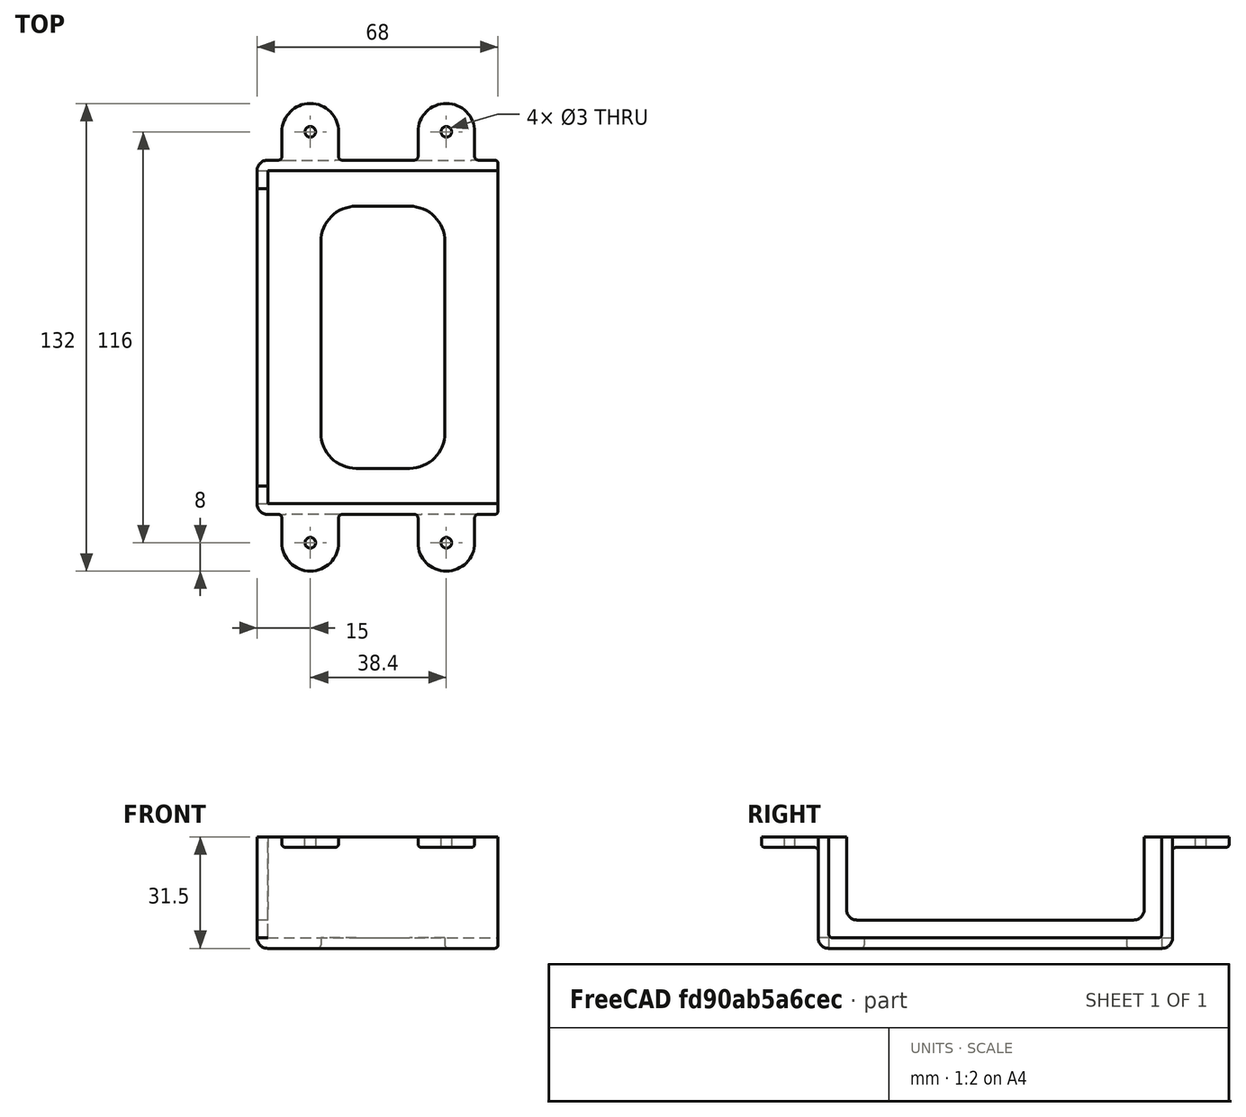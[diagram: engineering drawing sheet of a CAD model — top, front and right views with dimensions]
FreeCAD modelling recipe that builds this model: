
FCSTD DOCUMENT  (FreeCAD 0.21R33668 +7 (Git))
Label: UnderTableBracket-4
License: All rights reserved
LicenseURL: http://en.wikipedia.org/wiki/All_rights_reserved
objects: Sketcher::SketchObject×3, PartDesign::Pocket×2, PartDesign::Fillet×2, Spreadsheet::Sheet×1, PartDesign::AdditiveBox×1, PartDesign::Thickness×1, PartDesign::LinearPattern×1, PartDesign::Plane×1, PartDesign::Mirrored×1, PartDesign::Pad×1, PartDesign::MultiTransform×1, PartDesign::Body×1, App::Part×1, Mesh::Feature×1
note: 22 computed .brp shape members not serialized (recipe doc carries the construction recipe); baked Part::Feature solids carry a one-line shape summary decoded from their .brp

FEATURE [Spreadsheet::Sheet] Spreadsheet
  cells = A1='Width; B1(Width)=94; A2='Height; B2(Height)=28.5; A3='Depth; B3(Depth)=65; A4='Screw Diameter; B4(ScrewDiameter)=3
FEATURE [PartDesign::AdditiveBox] Box
  AttacherType = Attacher::AttachEngine3D
  Height = 28.5
  Length = 65
  Width = 94
  expr: Height = Spreadsheet.Height
  expr: Length = Spreadsheet.Depth
  expr: Width = Spreadsheet.Width
FEATURE [PartDesign::Thickness] Thickness
  Base = -> Box [Face6,Face2]
  BaseFeature = -> Box
  Intersection = false
  Join = 0
  Mode = 0
  SupportTransform = false
  Value = 3
FEATURE [Sketcher::SketchObject] Sketch
  ExternalGeometry = -> [Thickness]
  FullyConstrained = false
  MapMode = 5
  Placement = pos=(0,0,0) rot=(0.57735,0.57735,0.57735;2.0944rad)
  Support = -> [Thickness]
  sketch-geometry (8):
    g0: LineSegment StartX=89 StartY=28.5 StartZ=0 EndX=89 EndY=8 EndZ=0
    g1: ArcOfCircle CenterX=86 CenterY=8 CenterZ=0 NormalX=0 NormalY=0 NormalZ=1 AngleXU=0 Radius=3 StartAngle=4.71239 EndAngle=6.28319
    g2: LineSegment StartX=86 StartY=5 StartZ=0 EndX=8 EndY=5 EndZ=0
    g3: ArcOfCircle CenterX=8 CenterY=8 CenterZ=0 NormalX=0 NormalY=0 NormalZ=1 AngleXU=0 Radius=3 StartAngle=3.14159 EndAngle=4.71239
    g4: LineSegment StartX=5 StartY=8 StartZ=0 EndX=5 EndY=28.5 EndZ=0
    g5: GeomPoint X=5 Y=35.516 Z=0
    g6: GeomPoint X=89 Y=5 Z=0
    g7: LineSegment StartX=5 StartY=28.5 StartZ=0 EndX=89 EndY=28.5 EndZ=0
  constraints (19):
    c: Tangent(g0,g1) = 1.5708
    c: Tangent(g1,g2) = 1.5708
    c: Tangent(g2,g3) = 1.5708
    c: Tangent(g3,g4) = 1.5708
    c: Horizontal(g2)
    c: Vertical(g0)
    c: Vertical(g4)
    c: Equal(g1,g3)
    c: PointOnObject(g5,g4)
    c: PointOnObject(g6,g0)
    c: PointOnObject(g6,g2)
    c: PointOnObject(g4,g-3)
    c: PointOnObject(g0,g-3)
    c: Radius(g3) = 3
    c: DistanceX(g-3,g4) = 5
    c: DistanceX(g0,g-3) = 5
    c: DistanceY(g-1,g2) = 5
    c: Coincident(g7,g4)
    c: Coincident(g7,g0)
FEATURE [PartDesign::Pocket] Pocket
  BaseFeature = -> Thickness
  Direction = (-1,0,0)
  Length = 5
  Length2 = 5
  Profile = -> Sketch
  ReferenceAxis = -> Sketch [N_Axis]
  Type = 1
FEATURE [Sketcher::SketchObject] Sketch001
  ExternalGeometry = -> [Pocket]
  FullyConstrained = true
  MapMode = 5
  Support = -> [Pocket]
  sketch-geometry (10):
    g0: ArcOfCircle CenterX=25 CenterY=74 CenterZ=0 NormalX=0 NormalY=0 NormalZ=1 AngleXU=0 Radius=10 StartAngle=1.5708 EndAngle=3.14159
    g1: LineSegment StartX=25 StartY=84 StartZ=0 EndX=40 EndY=84 EndZ=0
    g2: ArcOfCircle CenterX=40 CenterY=74 CenterZ=0 NormalX=0 NormalY=0 NormalZ=1 AngleXU=0 Radius=10 StartAngle=-9e-16 EndAngle=1.5708
    g3: LineSegment StartX=50 StartY=74 StartZ=0 EndX=50 EndY=20 EndZ=0
    g4: ArcOfCircle CenterX=40 CenterY=20 CenterZ=0 NormalX=0 NormalY=0 NormalZ=1 AngleXU=0 Radius=10 StartAngle=4.71239 EndAngle=6.28319
    g5: LineSegment StartX=40 StartY=10 StartZ=0 EndX=25 EndY=10 EndZ=0
    g6: ArcOfCircle CenterX=25 CenterY=20 CenterZ=0 NormalX=0 NormalY=0 NormalZ=1 AngleXU=0 Radius=10 StartAngle=3.14159 EndAngle=4.71239
    g7: LineSegment StartX=15 StartY=20 StartZ=0 EndX=15 EndY=74 EndZ=0
    g8: GeomPoint X=15 Y=84 Z=0
    g9: GeomPoint X=50 Y=10 Z=0
  constraints (24):
    c: Tangent(g0,g1) = 1.5708
    c: Tangent(g1,g2) = 1.5708
    c: Tangent(g2,g3) = 1.5708
    c: Tangent(g3,g4) = 1.5708
    c: Tangent(g4,g5) = 1.5708
    c: Tangent(g5,g6) = 1.5708
    c: Tangent(g6,g7) = 1.5708
    c: Tangent(g7,g0) = 1.5708
    c: Horizontal(g1)
    c: Horizontal(g5)
    c: Vertical(g3)
    c: Vertical(g7)
    c: Equal(g0,g2)
    c: Equal(g2,g4)
    c: Equal(g4,g6)
    c: PointOnObject(g8,g1)
    c: PointOnObject(g8,g7)
    c: PointOnObject(g9,g3)
    c: PointOnObject(g9,g5)
    c: Radius(g2) = 10
    c: DistanceY(g1,g-4) = 10
    c: DistanceY(g-4,g4) = 10
    c: DistanceX(g3,g-4) = 15
    c: DistanceX(g-3,g0) = 15
FEATURE [Sketcher::SketchObject] Sketch002
  ExternalGeometry = -> [Box]
  FullyConstrained = true
  MapMode = 5
  Placement = pos=(0,0,28.5) rot=(0,0,1;0rad)
  Support = -> [Box]
  expr: Constraints[10] = Spreadsheet.ScrewDiameter
  sketch-geometry (5):
    g0: ArcOfCircle CenterX=12 CenterY=105 CenterZ=0 NormalX=0 NormalY=0 NormalZ=1 AngleXU=0 Radius=8 StartAngle=1e-16 EndAngle=3.14159
    g1: LineSegment StartX=4 StartY=105 StartZ=0 EndX=4 EndY=94 EndZ=0
    g2: LineSegment StartX=20 StartY=94 StartZ=0 EndX=20 EndY=105 EndZ=0
    g3: Circle CenterX=12 CenterY=105 CenterZ=0 NormalX=0 NormalY=0 NormalZ=1 AngleXU=0 Radius=1.5
    g4: LineSegment StartX=4 StartY=94 StartZ=0 EndX=20 EndY=94 EndZ=0
  constraints (13):
    c: Tangent(g0,g1) = -1.5708
    c: Tangent(g2,g0) = -1.5708
    c: Vertical(g1)
    c: PointOnObject(g1,g-3)
    c: PointOnObject(g2,g-3)
    c: Radius(g0) = 8
    c: Vertical(g2)
    c: DistanceY(g2,g2) = 11
    c: DistanceX(g-3,g1) = 4
    c: Coincident(g3,g0)
    c: Diameter(g3) = 3
    c: Coincident(g4,g1)
    c: Coincident(g4,g2)
FEATURE [PartDesign::LinearPattern] LinearPattern
  Direction = -> Sketch002 [H_Axis]
  Length = 38.4
  Occurrences = 2
FEATURE [PartDesign::Plane] DatumPlane
  AttachmentOffset = pos=(0,0,0) rot=(-0.57735,0.57735,0.57735;2.0944rad)
  Length = 67.378
  MapMode = 45
  Placement = pos=(32.5,47,14.25) rot=(-0.57735,0.57735,0.57735;2.0944rad)
  ResizeMode = 0
  Support = -> [Box]
  Width = 103.878
FEATURE [PartDesign::Mirrored] Mirrored
  MirrorPlane = -> DatumPlane
FEATURE [PartDesign::Pocket] Pocket001
  BaseFeature = -> Pocket
  Direction = (0,0,-1)
  Length = 5
  Length2 = 5
  Profile = -> Sketch001
  ReferenceAxis = -> Sketch001 [N_Axis]
  Type = 1
FEATURE [PartDesign::Fillet] Fillet
  Base = -> Pocket001 [Edge32,Edge34]
  BaseFeature = -> Pocket001
  Radius = 1
  SupportTransform = false
  UseAllEdges = false
FEATURE [PartDesign::Pad] Pad
  BaseFeature = -> Fillet
  Direction = (0,0,1)
  Length = 3
  Length2 = 10
  Profile = -> Sketch002
  ReferenceAxis = -> Sketch002 [N_Axis]
  Reversed = true
  Type = 0
FEATURE [PartDesign::MultiTransform] MultiTransform
  BaseFeature = -> Pad
  Originals = -> [Pad]
  Transformations = -> [LinearPattern,Mirrored]
FEATURE [PartDesign::Fillet] Fillet001
  Base = -> MultiTransform [Edge97,Edge100,Edge101,Edge104,Edge105,Edge108,Edge109,Edge95,Edge123,Edge168,Edge169,Edge167,Edge120,Edge161,Edge162,Edge160,Edge121,Edge124,Edge122,Edge119,Edge73,Edge72,Edge70,Edge69,Edge68,Edge87,Edge88,Edge137,Edge139,Edge138,Edge90,Edge91,Edge145,Edge147,Edge146,Edge89,Edge92]
  BaseFeature = -> MultiTransform
  Radius = 1
  SupportTransform = false
  UseAllEdges = false
FEATURE [PartDesign::Body] Body
  Group = -> [Box,Thickness,Sketch,Pocket,Sketch001,Pocket001,Fillet,Sketch002,Pad,MultiTransform,LinearPattern,DatumPlane,Mirrored,Fillet001]
  Origin = -> Origin001
  Tip = -> Fillet001
FEATURE [App::Part] Part  label="Bracket"
  Group = -> [Body]
  Origin = -> Origin
FEATURE [Mesh::Feature] Mesh  label="Bracket (Meshed)"
